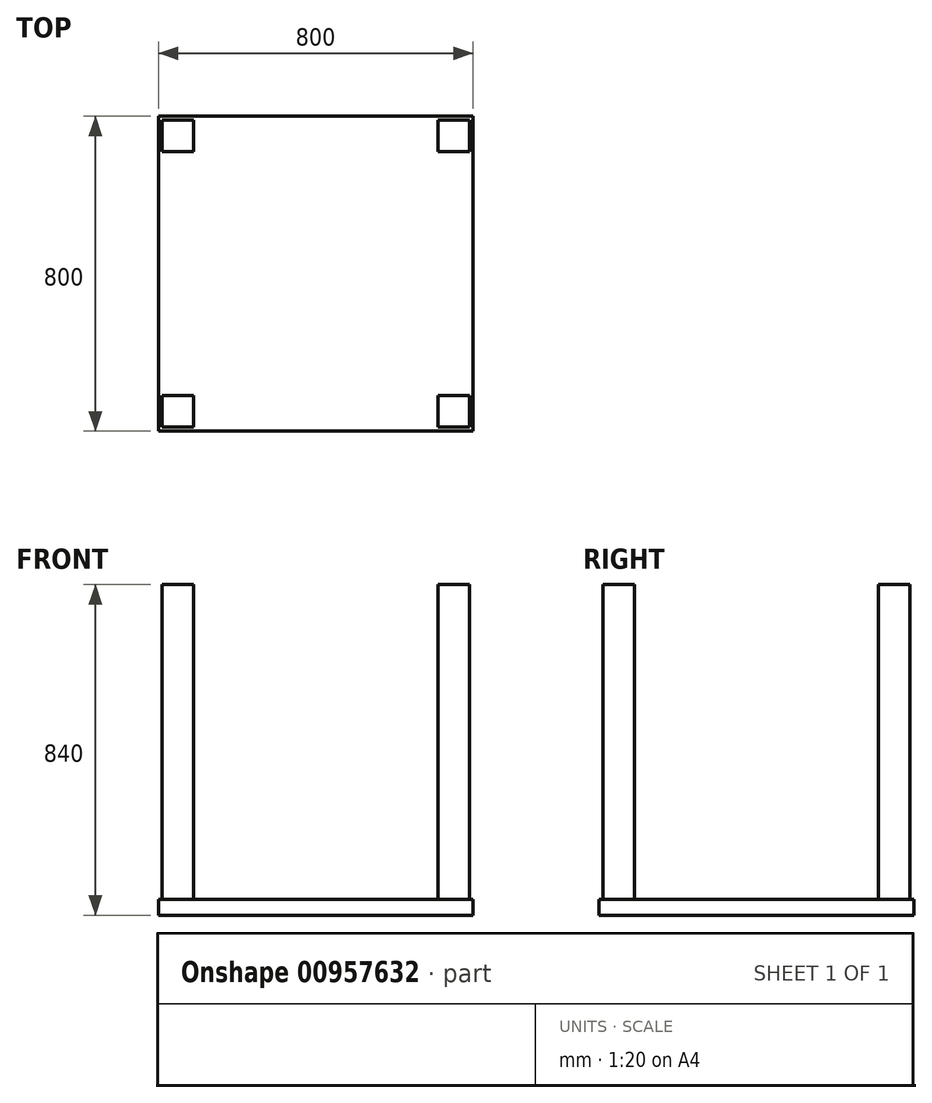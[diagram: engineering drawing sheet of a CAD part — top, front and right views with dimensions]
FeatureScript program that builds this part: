
annotation { "Feature Type Name" : "Feature", "Feature Type Description" : "" }
export const myFeature = defineFeature(function(context is Context, id is Id, definition is map)
    precondition{}
    {
        {
            var Q0;
            Q0=qCreatedBy(makeId("Top.planeOp"),FACE);
            var sketch = newSketch(context, id + "F0", { "sketchPlane" : qUnion([Q0])});
            skLineSegment(sketch, "E0.bottom", {"start": v(-400, 400) * mm, "end": v(400, 400) * mm});
            skLineSegment(sketch, "E0.top", {"start": v(-400, -400) * mm, "end": v(400, -400) * mm});
            skLineSegment(sketch, "E0.left", {"start": v(-400, 400) * mm, "end": v(-400, -400) * mm});
            skLineSegment(sketch, "E0.right", {"start": v(400, 400) * mm, "end": v(400, -400) * mm});
            skPoint(sketch, "E0.middle", {"position": v(0, 0) * mm});
            skSolve(sketch);
        }
        {
            var Q0;
            Q0=makeQuery(id+"F0.imprint","IMPRINT",FACE,{"disambiguationData":[TD([[makeQuery(id+"F0.imprint","IMPRINT",EDGE,{"derivedFrom":sQuery(id+"F0.wireOp",EDGE,"E0.bottom")}),-1.0]])]});
            extrude(context, id + "F1", {"entities" : qUnion([Q0]), "depth" : 40 * mm, "offsetDistance" : 25 * mm});
        }
        {
            var Q0;
            Q0=makeQuery(id+"F1.opExtrude","CAP_FACE",FACE,{"disambiguationData":[OSD([sQuery(id+"F0.wireOp",EDGE,"E0.bottom"),sQuery(id+"F0.wireOp",EDGE,"E0.top"),sQuery(id+"F0.wireOp",EDGE,"E0.left"),sQuery(id+"F0.wireOp",EDGE,"E0.right")])],"isStart":false});
            var sketch = newSketch(context, id + "F2", { "sketchPlane" : qUnion([Q0])});
            skLineSegment(sketch, "E1.bottom", {"start": v(-390, 390) * mm, "end": v(-310, 390) * mm});
            skLineSegment(sketch, "E1.top", {"start": v(-390, 310) * mm, "end": v(-310, 310) * mm});
            skLineSegment(sketch, "E1.left", {"start": v(-390, 390) * mm, "end": v(-390, 310) * mm});
            skLineSegment(sketch, "E1.right", {"start": v(-310, 390) * mm, "end": v(-310, 310) * mm});
            skLineSegment(sketch, "E2.MirrorCS", {"start": v(390, 390) * mm, "end": v(310, 390) * mm});
            skLineSegment(sketch, "E3.MirrorCS", {"start": v(390, 390) * mm, "end": v(390, 310) * mm});
            skLineSegment(sketch, "E4.MirrorCS", {"start": v(310, 390) * mm, "end": v(310, 310) * mm});
            skLineSegment(sketch, "E5.MirrorCS", {"start": v(390, 310) * mm, "end": v(310, 310) * mm});
            skLineSegment(sketch, "E6.MirrorCS", {"start": v(-390, -390) * mm, "end": v(-390, -310) * mm});
            skLineSegment(sketch, "E7.MirrorCS", {"start": v(-390, -310) * mm, "end": v(-310, -310) * mm});
            skLineSegment(sketch, "E8.MirrorCS", {"start": v(390, -390) * mm, "end": v(390, -310) * mm});
            skLineSegment(sketch, "E9.MirrorCS", {"start": v(390, -310) * mm, "end": v(310, -310) * mm});
            skLineSegment(sketch, "E10.MirrorCS", {"start": v(-390, -390) * mm, "end": v(-310, -390) * mm});
            skLineSegment(sketch, "E11.MirrorCS", {"start": v(390, -390) * mm, "end": v(310, -390) * mm});
            skLineSegment(sketch, "E12.MirrorCS", {"start": v(310, -390) * mm, "end": v(310, -310) * mm});
            skLineSegment(sketch, "E13.MirrorCS", {"start": v(-310, -390) * mm, "end": v(-310, -310) * mm});
            skSolve(sketch);
        }
        {
            var Q0;
            Q0=makeQuery(id+"F2.imprint","IMPRINT",FACE,{"disambiguationData":[TD([[makeQuery(id+"F2.imprint","IMPRINT",EDGE,{"derivedFrom":sQuery(id+"F2.wireOp",EDGE,"E1.bottom")}),-1.0]])]});
            var Q1;
            Q1=makeQuery(id+"F2.imprint","IMPRINT",FACE,{"disambiguationData":[TD([[makeQuery(id+"F2.imprint","IMPRINT",EDGE,{"derivedFrom":sQuery(id+"F2.wireOp",EDGE,"E2.MirrorCS")}),1.0]])]});
            var Q2;
            Q2=makeQuery(id+"F2.imprint","IMPRINT",FACE,{"disambiguationData":[TD([[makeQuery(id+"F2.imprint","IMPRINT",EDGE,{"derivedFrom":sQuery(id+"F2.wireOp",EDGE,"E8.MirrorCS")}),1.0]])]});
            var Q3;
            Q3=makeQuery(id+"F2.imprint","IMPRINT",FACE,{"disambiguationData":[TD([[makeQuery(id+"F2.imprint","IMPRINT",EDGE,{"derivedFrom":sQuery(id+"F2.wireOp",EDGE,"E6.MirrorCS")}),-1.0]])]});
            extrude(context, id + "F3", {"entities" : qUnion([Q0, Q1, Q2, Q3]), "operationType" : NewBodyOperationType.ADD, "depth" : 800 * mm, "offsetDistance" : 25 * mm});
        }
    });
